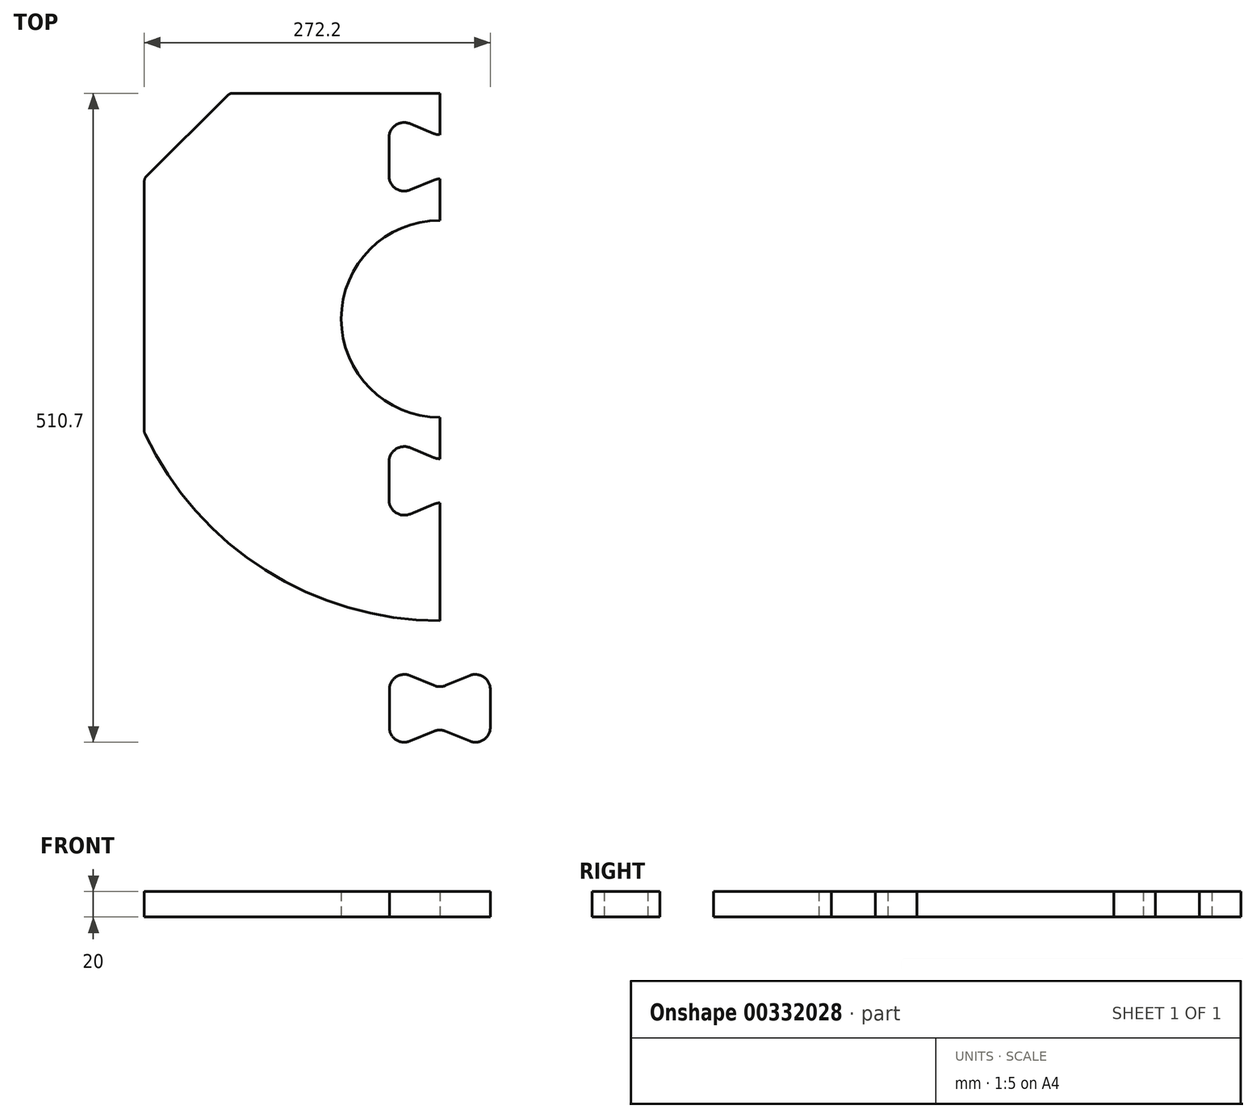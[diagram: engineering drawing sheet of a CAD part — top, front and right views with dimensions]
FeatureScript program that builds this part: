
annotation { "Feature Type Name" : "Feature", "Feature Type Description" : "" }
export const myFeature = defineFeature(function(context is Context, id is Id, definition is map)
    precondition{}
    {
        {
            var Q0;
            Q0=qCreatedBy(makeId("Top.planeOp"),FACE);
            var sketch = newSketch(context, id + "F0", { "sketchPlane" : qUnion([Q0])});
            skArc(sketch, "E0", {"start": v(0, -77.5) * mm, "mid": v(-77.5, 0) * mm, "end": v(0, 77.5) * mm});
            skLineSegment(sketch, "E1", {"start": v(0, 177.5) * mm, "end": v(-163.09, 177.5) * mm});
            skLineSegment(sketch, "E2", {"start": v(-166.61, 176.04) * mm, "end": v(-231.03, 111.97) * mm});
            skLineSegment(sketch, "E3", {"start": v(-232.5, 108.42) * mm, "end": v(-232.5, -88.38) * mm});
            skArc(sketch, "E4", {"start": v(0, -237.5) * mm, "mid": v(-137.33, -197.66) * mm, "end": v(-232.02, -90.52) * mm});
            skLineSegment(sketch, "E5", {"start": v(-232.5, -89.5) * mm, "end": v(0, -89.5) * mm, "construction": true});
            skLineSegment(sketch, "E6", {"start": v(0, 127.5) * mm, "end": v(-40, 127.5) * mm, "construction": true});
            skArc(sketch, "E7", {"start": v(-40, 142.5) * mm, "mid": v(-34.67, 152.48) * mm, "end": v(-23.4, 153.59) * mm});
            skArc(sketch, "E8", {"start": v(0, 144.88) * mm, "mid": v(-2.34, 145.11) * mm, "end": v(-4.6, 145.8) * mm});
            skLineSegment(sketch, "E9", {"start": v(-4.6, 145.8) * mm, "end": v(-23.4, 153.59) * mm});
            skArc(sketch, "E10.MirrorCS", {"start": v(-40, 112.5) * mm, "mid": v(-34.67, 102.52) * mm, "end": v(-23.4, 101.41) * mm});
            skLineSegment(sketch, "E11.MirrorCS", {"start": v(-4.6, 109.2) * mm, "end": v(-23.4, 101.41) * mm});
            skArc(sketch, "E12.MirrorCS", {"start": v(0, 110.12) * mm, "mid": v(-2.34, 109.89) * mm, "end": v(-4.6, 109.2) * mm});
            skLineSegment(sketch, "E13", {"start": v(-40, 142.5) * mm, "end": v(-40, 112.5) * mm});
            skLineSegment(sketch, "E14", {"start": v(0, 0) * mm, "end": v(-77.5, 0) * mm, "construction": true});
            skLineSegment(sketch, "E15.MirrorCS", {"start": v(-4.6, -145.8) * mm, "end": v(-23.4, -153.59) * mm});
            skArc(sketch, "E16.MirrorCS", {"start": v(-40, -142.5) * mm, "mid": v(-34.67, -152.48) * mm, "end": v(-23.4, -153.59) * mm});
            skLineSegment(sketch, "E17.MirrorCS", {"start": v(-40, -142.5) * mm, "end": v(-40, -112.5) * mm});
            skArc(sketch, "E18.MirrorCS", {"start": v(-40, -112.5) * mm, "mid": v(-34.67, -102.52) * mm, "end": v(-23.4, -101.41) * mm});
            skLineSegment(sketch, "E19.MirrorCS", {"start": v(-4.6, -109.2) * mm, "end": v(-23.4, -101.41) * mm});
            skArc(sketch, "E20.MirrorCS", {"start": v(0, -110.12) * mm, "mid": v(-2.34, -109.89) * mm, "end": v(-4.6, -109.2) * mm});
            skArc(sketch, "E21.MirrorCS", {"start": v(0, -144.88) * mm, "mid": v(-2.34, -145.11) * mm, "end": v(-4.6, -145.8) * mm});
            skLineSegment(sketch, "E22", {"start": v(0, -144.88) * mm, "end": v(0, -237.5) * mm});
            skLineSegment(sketch, "E23", {"start": v(0, 177.5) * mm, "end": v(0, 144.88) * mm});
            skLineSegment(sketch, "E24", {"start": v(0, 110.12) * mm, "end": v(0, 77.5) * mm});
            skLineSegment(sketch, "E25", {"start": v(0, 177.5) * mm, "end": v(0, 77.5) * mm, "construction": true});
            skLineSegment(sketch, "E26", {"start": v(0, -110.12) * mm, "end": v(0, -77.5) * mm});
            skLineSegment(sketch, "E27", {"start": v(0, -77.5) * mm, "end": v(0, -237.5) * mm, "construction": true});
            skLineSegment(sketch, "E28.MirrorCS", {"start": v(-4.6, -324.8) * mm, "end": v(-23.4, -332.59) * mm, "construction": true});
            skArc(sketch, "E29.MirrorCS", {"start": v(-40, -321.5) * mm, "mid": v(-34.67, -331.48) * mm, "end": v(-23.4, -332.59) * mm, "construction": true});
            skLineSegment(sketch, "E30.MirrorCS", {"start": v(-40, -321.5) * mm, "end": v(-40, -291.5) * mm, "construction": true});
            skArc(sketch, "E31.MirrorCS", {"start": v(-40, -291.5) * mm, "mid": v(-34.67, -281.52) * mm, "end": v(-23.4, -280.41) * mm, "construction": true});
            skLineSegment(sketch, "E32.MirrorCS", {"start": v(-4.6, -288.2) * mm, "end": v(-23.4, -280.41) * mm, "construction": true});
            skArc(sketch, "E33.MirrorCS", {"start": v(0, -289.12) * mm, "mid": v(-2.34, -288.89) * mm, "end": v(-4.6, -288.2) * mm, "construction": true});
            skArc(sketch, "E34.MirrorCS", {"start": v(0, -323.88) * mm, "mid": v(-2.34, -324.11) * mm, "end": v(-4.6, -324.8) * mm, "construction": true});
            skArc(sketch, "E35.MirrorCS", {"start": v(0, -323.88) * mm, "mid": v(2.34, -324.11) * mm, "end": v(4.6, -324.8) * mm, "construction": true});
            skArc(sketch, "E36.MirrorCS", {"start": v(0, -289.12) * mm, "mid": v(2.34, -288.89) * mm, "end": v(4.6, -288.2) * mm, "construction": true});
            skArc(sketch, "E37.MirrorCS", {"start": v(40, -291.5) * mm, "mid": v(34.67, -281.52) * mm, "end": v(23.4, -280.41) * mm, "construction": true});
            skArc(sketch, "E38.MirrorCS", {"start": v(40, -321.5) * mm, "mid": v(34.67, -331.48) * mm, "end": v(23.4, -332.59) * mm, "construction": true});
            skLineSegment(sketch, "E39.MirrorCS", {"start": v(4.6, -288.2) * mm, "end": v(23.4, -280.41) * mm, "construction": true});
            skLineSegment(sketch, "E40.MirrorCS", {"start": v(40, -321.5) * mm, "end": v(40, -291.5) * mm, "construction": true});
            skLineSegment(sketch, "E41.MirrorCS", {"start": v(4.6, -324.8) * mm, "end": v(23.4, -332.59) * mm, "construction": true});
            skArc(sketch, "E42.0", {"start": v(0, -289.42) * mm, "mid": v(2.4, -289.18) * mm, "end": v(4.7, -288.48) * mm});
            skArc(sketch, "E42.1", {"start": v(0, -289.42) * mm, "mid": v(-2.4, -289.18) * mm, "end": v(-4.7, -288.48) * mm});
            skLineSegment(sketch, "E42.2", {"start": v(-4.7, -288.48) * mm, "end": v(-23.52, -280.7) * mm});
            skLineSegment(sketch, "E42.3", {"start": v(4.7, -324.52) * mm, "end": v(23.52, -332.3) * mm});
            skArc(sketch, "E42.4", {"start": v(39.7, -321.5) * mm, "mid": v(34.5, -331.23) * mm, "end": v(23.52, -332.3) * mm});
            skLineSegment(sketch, "E42.5", {"start": v(39.7, -321.5) * mm, "end": v(39.7, -291.5) * mm});
            skArc(sketch, "E42.6", {"start": v(39.7, -291.5) * mm, "mid": v(34.5, -281.77) * mm, "end": v(23.52, -280.7) * mm});
            skArc(sketch, "E42.7", {"start": v(0, -323.58) * mm, "mid": v(2.4, -323.82) * mm, "end": v(4.7, -324.52) * mm});
            skArc(sketch, "E42.8", {"start": v(0, -323.58) * mm, "mid": v(-2.4, -323.82) * mm, "end": v(-4.7, -324.52) * mm});
            skLineSegment(sketch, "E42.9", {"start": v(-4.7, -324.52) * mm, "end": v(-23.52, -332.3) * mm});
            skLineSegment(sketch, "E42.10", {"start": v(4.7, -288.48) * mm, "end": v(23.52, -280.7) * mm});
            skArc(sketch, "E42.11", {"start": v(-39.7, -321.5) * mm, "mid": v(-34.5, -331.23) * mm, "end": v(-23.52, -332.3) * mm});
            skLineSegment(sketch, "E42.12", {"start": v(-39.7, -321.5) * mm, "end": v(-39.7, -291.5) * mm});
            skArc(sketch, "E42.13", {"start": v(-39.7, -291.5) * mm, "mid": v(-34.5, -281.77) * mm, "end": v(-23.52, -280.7) * mm});
            skPoint(sketch, "E43.visualSharp", {"position": v(-232.5, -89.5) * mm});
            skArc(sketch, "E43.filletArc", {"start": v(-232.5, -88.38) * mm, "mid": v(-232.38, -89.48) * mm, "end": v(-232.02, -90.52) * mm});
            skPoint(sketch, "E44.visualSharp", {"position": v(-232.5, 110.5) * mm});
            skArc(sketch, "E44.filletArc", {"start": v(-231.03, 111.97) * mm, "mid": v(-232.12, 110.34) * mm, "end": v(-232.5, 108.42) * mm});
            skPoint(sketch, "E45.visualSharp", {"position": v(-165.15, 177.5) * mm});
            skArc(sketch, "E45.filletArc", {"start": v(-163.09, 177.5) * mm, "mid": v(-165, 177.12) * mm, "end": v(-166.61, 176.04) * mm});
            skSolve(sketch);
        }
        {
            var Q0;
            Q0 = qSketchRegion(id + "F0", true);
            extrude(context, id + "F1", {"entities" : qUnion([Q0]), "depth" : 20 * mm});
        }
    });
